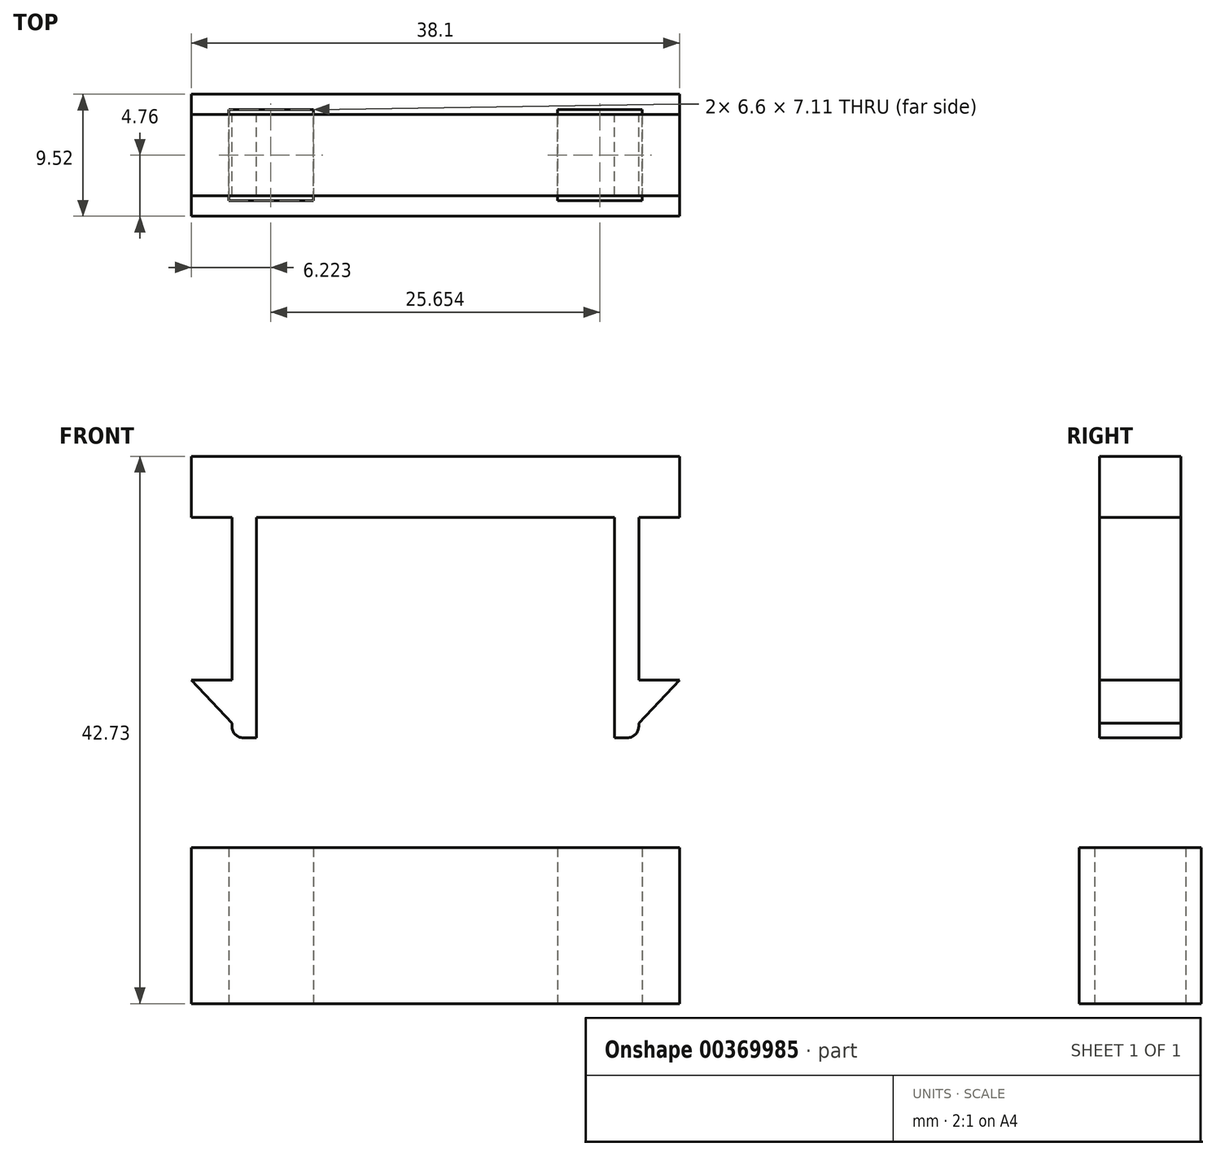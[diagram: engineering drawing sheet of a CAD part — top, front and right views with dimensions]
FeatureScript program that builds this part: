
annotation { "Feature Type Name" : "Feature", "Feature Type Description" : "" }
export const myFeature = defineFeature(function(context is Context, id is Id, definition is map)
    precondition{}
    {
        {
            var Q0;
            Q0=qCreatedBy(makeId("Front.planeOp"),FACE);
            var sketch = newSketch(context, id + "F0", { "sketchPlane" : qUnion([Q0])});
            skLineSegment(sketch, "E0.bottom", {"start": v(0, 0) * mm, "end": v(3.18, 0) * mm});
            skLineSegment(sketch, "E0.top", {"start": v(0, 4.76) * mm, "end": v(38.1, 4.76) * mm});
            skLineSegment(sketch, "E0.left", {"start": v(0, 0) * mm, "end": v(0, 4.76) * mm});
            skLineSegment(sketch, "E0.right", {"start": v(38.1, 0) * mm, "end": v(38.1, 4.76) * mm});
            skLineSegment(sketch, "E1", {"start": v(3.18, 0) * mm, "end": v(3.18, -12.7) * mm});
            skLineSegment(sketch, "E2", {"start": v(3.18, -12.7) * mm, "end": v(0, -12.7) * mm});
            skLineSegment(sketch, "E3", {"start": v(0, -12.7) * mm, "end": v(3.18, -16.07) * mm});
            skLineSegment(sketch, "E4", {"start": v(3.18, -16.07) * mm, "end": v(3.18, -16.33) * mm});
            skLineSegment(sketch, "E5", {"start": v(4.06, -17.21) * mm, "end": v(5.08, -17.21) * mm});
            skLineSegment(sketch, "E6", {"start": v(5.08, -17.21) * mm, "end": v(5.08, 0) * mm});
            skLineSegment(sketch, "E7", {"start": v(19.05, 0) * mm, "end": v(19.05, -24.94) * mm, "construction": true});
            skLineSegment(sketch, "E8.MirrorCS", {"start": v(33.02, -17.21) * mm, "end": v(33.02, 0) * mm});
            skLineSegment(sketch, "E9.MirrorCS", {"start": v(34.04, -17.21) * mm, "end": v(33.02, -17.21) * mm});
            skLineSegment(sketch, "E10.MirrorCS", {"start": v(34.93, -16.07) * mm, "end": v(34.93, -16.33) * mm});
            skLineSegment(sketch, "E11.MirrorCS", {"start": v(38.1, -12.7) * mm, "end": v(34.93, -16.07) * mm});
            skLineSegment(sketch, "E12.MirrorCS", {"start": v(34.93, -12.7) * mm, "end": v(38.1, -12.7) * mm});
            skLineSegment(sketch, "E13.MirrorCS", {"start": v(34.93, 0) * mm, "end": v(34.93, -12.7) * mm});
            skLineSegment(sketch, "E14.trimOffspring", {"start": v(5.08, 0) * mm, "end": v(33.02, 0) * mm});
            skPoint(sketch, "E15.visualSharp", {"position": v(3.18, -17.21) * mm});
            skArc(sketch, "E15.filletArc", {"start": v(3.18, -16.33) * mm, "mid": v(3.44, -16.95) * mm, "end": v(4.06, -17.21) * mm});
            skPoint(sketch, "E16.visualSharp", {"position": v(34.92, -17.21) * mm});
            skArc(sketch, "E16.filletArc", {"start": v(34.04, -17.21) * mm, "mid": v(34.66, -16.95) * mm, "end": v(34.92, -16.33) * mm});
            skLineSegment(sketch, "E17", {"start": v(3.18, -12.7) * mm, "end": v(3.18, -42.56) * mm, "construction": true});
            skLineSegment(sketch, "E18", {"start": v(34.93, -12.7) * mm, "end": v(34.93, -42.56) * mm, "construction": true});
            skLineSegment(sketch, "E19", {"start": v(0, 0) * mm, "end": v(0, -58.91) * mm, "construction": true});
            skPoint(sketch, "E19.endSnap0", {"position": v(0, 2.38) * mm});
            skLineSegment(sketch, "E20", {"start": v(38.1, 0) * mm, "end": v(38.1, -59.66) * mm, "construction": true});
            skLineSegment(sketch, "E21.bottom", {"start": v(0, -25.78) * mm, "end": v(38.1, -25.78) * mm});
            skLineSegment(sketch, "E21.top", {"start": v(0, -37.97) * mm, "end": v(38.1, -37.97) * mm});
            skLineSegment(sketch, "E21.left", {"start": v(0, -25.78) * mm, "end": v(0, -37.97) * mm});
            skLineSegment(sketch, "E21.right", {"start": v(38.1, -25.78) * mm, "end": v(38.1, -37.97) * mm});
            skLineSegment(sketch, "E22.trimOffspring", {"start": v(34.93, 0) * mm, "end": v(38.1, 0) * mm});
            skSolve(sketch);
        }
        {
            var Q0;
            Q0=makeQuery(id+"F0.imprint","IMPRINT",FACE,{"disambiguationData":[TD([[makeQuery(id+"F0.imprint","IMPRINT",EDGE,{"derivedFrom":sQuery(id+"F0.wireOp",EDGE,"E0.bottom")}),1.0]])]});
            extrude(context, id + "F1", {"entities" : qUnion([Q0]), "endBound" : BoundingType.SYMMETRIC, "depth" : 6.35 * mm, "offsetDistance" : 25.4 * mm});
        }
        {
            var Q0;
            Q0=makeQuery(id+"F0.imprint","IMPRINT",FACE,{"disambiguationData":[TD([[makeQuery(id+"F0.imprint","IMPRINT",EDGE,{"derivedFrom":sQuery(id+"F0.wireOp",EDGE,"E21.bottom")}),-1.0]])]});
            extrude(context, id + "F2", {"entities" : qUnion([Q0]), "endBound" : BoundingType.SYMMETRIC, "depth" : 9.52 * mm, "offsetDistance" : 25.4 * mm});
        }
        {
            var Q0;
            Q0=makeQuery(id+"F2.opExtrude","SWEPT_FACE",FACE,{"disambiguationData":[OSD([sQuery(id+"F0.wireOp",EDGE,"E21.top")])]});
            var sketch = newSketch(context, id + "F3", { "sketchPlane" : qUnion([Q0])});
            skLineSegment(sketch, "E23.bottom", {"start": v(2.92, 3.56) * mm, "end": v(9.53, 3.56) * mm});
            skLineSegment(sketch, "E23.top", {"start": v(2.92, -3.56) * mm, "end": v(9.53, -3.56) * mm});
            skLineSegment(sketch, "E23.left", {"start": v(2.92, 3.56) * mm, "end": v(2.92, -3.56) * mm});
            skLineSegment(sketch, "E23.right", {"start": v(9.53, 3.56) * mm, "end": v(9.53, -3.56) * mm});
            skLineSegment(sketch, "E24.bottom", {"start": v(2.92, 3.56) * mm, "end": v(2.92, 3.56) * mm});
            skLineSegment(sketch, "E24.top", {"start": v(2.92, 4.76) * mm, "end": v(2.92, 4.76) * mm});
            skLineSegment(sketch, "E24.left", {"start": v(2.92, 3.56) * mm, "end": v(2.92, 4.76) * mm, "construction": true});
            skLineSegment(sketch, "E24.right", {"start": v(2.92, 3.56) * mm, "end": v(2.92, 4.76) * mm, "construction": true});
            skLineSegment(sketch, "E25.bottom", {"start": v(2.92, -3.56) * mm, "end": v(2.92, -3.56) * mm});
            skLineSegment(sketch, "E25.top", {"start": v(2.92, -4.76) * mm, "end": v(2.92, -4.76) * mm});
            skLineSegment(sketch, "E25.left", {"start": v(2.92, -3.56) * mm, "end": v(2.92, -4.76) * mm, "construction": true});
            skLineSegment(sketch, "E25.right", {"start": v(2.92, -3.56) * mm, "end": v(2.92, -4.76) * mm, "construction": true});
            skLineSegment(sketch, "E26", {"start": v(0, 0) * mm, "end": v(6.6, 0) * mm, "construction": true});
            skPoint(sketch, "E26.endSnap0", {"position": v(9.53, 0) * mm});
            skLineSegment(sketch, "E27", {"start": v(19.05, 4.76) * mm, "end": v(19.05, -4.76) * mm, "construction": true});
            skLineSegment(sketch, "E28.MirrorCS", {"start": v(35.18, 3.56) * mm, "end": v(28.58, 3.56) * mm});
            skLineSegment(sketch, "E29.MirrorCS", {"start": v(28.58, 3.56) * mm, "end": v(28.58, -3.56) * mm});
            skLineSegment(sketch, "E30.MirrorCS", {"start": v(35.18, -3.56) * mm, "end": v(28.58, -3.56) * mm});
            skLineSegment(sketch, "E31.MirrorCS", {"start": v(35.18, 3.56) * mm, "end": v(35.18, -3.56) * mm});
            skSolve(sketch);
        }
        {
            var Q0;
            Q0=makeQuery(id+"F3.imprint","IMPRINT",FACE,{"disambiguationData":[TD([[makeQuery(id+"F3.imprint","IMPRINT",EDGE,{"derivedFrom":sQuery(id+"F3.wireOp",EDGE,"E23.bottom")}),-1.0]])]});
            var Q1;
            Q1=makeQuery(id+"F3.imprint","IMPRINT",FACE,{"disambiguationData":[TD([[makeQuery(id+"F3.imprint","IMPRINT",EDGE,{"derivedFrom":sQuery(id+"F3.wireOp",EDGE,"E28.MirrorCS")}),1.0]])]});
            extrude(context, id + "F4", {"entities" : qUnion([Q0, Q1]), "operationType" : NewBodyOperationType.REMOVE, "oppositeDirection" : true, "depth" : 12.95 * mm, "offsetDistance" : 25.4 * mm});
        }
    });
